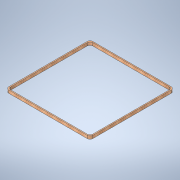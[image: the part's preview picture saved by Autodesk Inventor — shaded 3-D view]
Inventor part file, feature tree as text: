
AUTODESK INVENTOR PART (.ipt)
format: ipt  version: 2022 (Build 260153000, 153)  size: 121,856 bytes
history: native  units: in
note: dims shown in document units (in); Inventor stores cm internally (conversion verified against a paired STEP export)
features: helix x1, extrude x1, sketch x1
ambient origin geometry x8: Origin, YZ Plane, XZ Plane, XY Plane, X Axis, Y Axis, Z Axis, Center Point
bodies: Solid1 (feature_tree)
feature tree (3):
  helix  "Coil5or6"  [1 undecoded]
  extrude  "Extrusion1"  Depth=78.3465in
  sketch  "Sketch1"  dims[d1=80.315in d2=78.3465in d3=78.3465in d4=2.7559in d5=2.7559in d6=0.0in]
note: 1 required parameter value undecoded (feature->parameter linkage not recoverable at this tier; creation-order binding heuristic only, values carry confidence <= 0.55)
